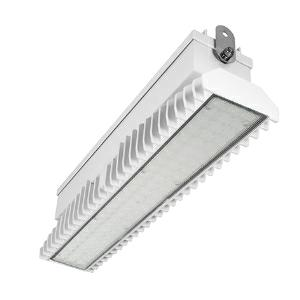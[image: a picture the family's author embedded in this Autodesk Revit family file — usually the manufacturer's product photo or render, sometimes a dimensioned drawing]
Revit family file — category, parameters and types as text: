
# Revit family: 3f_filippi_-_3f_lem_concentrato_3f_filippi_-_58887_a0812_-_3f_lem_1_led_50_cr_conc___vs_6c7b
name_source: partatom
category: Lighting Fixtures
units: mm (PartAtom-declared; Revit-internal decimal feet)

## family parameters
Cut with Voids When Loaded = No
Host = Face
Light Source = No
Part Type = Normal
Room Calculation Point = No
Round Connector Dimension = Use Diameter
Shared = No

## types (1)
- 3F Filippi - 3F LEM Concentrato (1 x LED, 6607 lm, 56 W, 4000 K)
    Apparent Load = 56 VA
    Approval mark = CE
    CIE Flux Codes = 78 93 98 100 100
    Color Rendering = 80
    Color Temperature = 4000 K
    Control Gear = Electronic ballast
    Default Elevation = 1800 mm
    Description = Industrial luminaire with high light output and high luminous efficiency designed with the most innovative technologies for environments with temperature up to 55°C.

ILLUMINOTECHNICAL
Luminous efficiency 100% (DLOR 98%, ULOR 2%).
Initial luminous flux of the luminaire 6607 lm.
Direct symmetric narrow distribution: the illuminated area has a elliptical shape.
Installation Interdistance Transv.D = 0.60 x hu - Long.D = 0.91 x hu.
Tabular UGR (CIE 117 - 4H-8H; S=0.25H; 70/50/20): RUG 23.3 - 24.5.
Beam angle: 38° - 61°.
Luminous efficacy 118 lm/W.
Lifetime (L93/B10): 30000 h. (tq+25°C)
Lifetime (L90/B10): 50000 h. (tq+25°C)
Lifetime (L85/B10): 80000 h. (tq+25°C)
Lifetime (L80/B10): 100000 h. (tq+25°C)
Lifetime (L85/B10): 50000 h. (tq+55°C)
Sudden decreased luminous flux after 50000 hours: 0% (C0).
Photobiological safety in compliance with IEC/TR 62778: RG0 risk exempt, (IEC 62471).
In compliance with IEC/EN 62722-2-1 - IEC/EN 62717 standards.

SOURCE
Mid-Power linear LED module 50W/840.
Energy efficiency class (UE 2019/2020 - UE 2019/2015): C.
CIE 13.3 Colour rendering index: CRI >80 (R9 <50%).
IES TM-30 Fidelity Index: Rf = 84 Rg = 95.
CCT nominal colour temperature 4000 K.
Colour initial tolerance (MacAdam): SDCM 3.

MECHANICAL
Passive modular heatsinks in die-casted aluminium, painted in white colour.
To optimize the thermal management of the LED module, the heatsinks are oversized and provided with self-cleaning of cooling fins.
Wiring body in aluminium and galvanised steel anchored solidly to the sinks and thermally separated.
3F Lens lenses with high luminous efficiency, transparent methacrylate (PMMA), fixed to the LED modules.
Fixing brackets in stainless steel.
Luminaire with limited surface temperature. - D - (EN 60598-2-24)
Dimensions: 542x115 mm, height 154 mm. Weight 6.385 kg.
IP65 protection degree.
Mechanical strength to impacts IK06 (1 joule).
Glow-wire test resistance 650°C.

ELECTRICAL
Halogen Free electronic wiring 230V-50/60Hz, power factor 0.95, THD <25%, constant output current, class I, 1 driver.
Power of the luminaire 56 W.
ENEC - CE.
SAFE FLICKER: PstLM=<1 and SVM=<0.4 (IEC TR 61547-1 and IEC TR 63158), to ensure a more comfortable and safe light.
Luminaire compliant with EN 60598-2-22 for power supply from a centralised emergency system CPSS (Central Power Supply System), not incorporated in the luminaire - high risk areas excluded. The default power and flux are 100% in AC and 100% in DC.
Ambient temperature from -30°C to +55°C.
Temperature class T6 max 85°C.
Quick connection via M20 3P connector with 9-13 mm tightening range.
Power unit positioned on a separate compartment by the LED module to ensure optimum temperatures of cabling components, to be inspectable and maintainable.
Relative humidity UR: <85%.

INSTALLATION
Ceiling / Suspended / Wall.
All accessories dedicated to this product are available on the Catalog and on our website www.3F-Filippi.com.

ACCESSORIES
A0812 - Anti-glare microprismatic VS moulded glass, tempered, not flammable, with sealing gasket.
One required for each light module. The pack contains 10 pieces.

APPLICATIONS
In commercial environments, exhibition and industrial areas, stores, open areas.
Applications with high ambient temperature up to 55°C.
Environments in which it is necessary a total protection against falling fragments (eg environments with foodstuffs or machines with moving parts or with extreme temperature changes), use luminaires with polycarbonate lenses.

WARNING
Fixture not suitable for cold stores with an ambient temperature <0°C and/or relative humidity >85%.
Luminaire designed for disposal/recycling at end-of-life.
Replaceable (LED only) light source by a professional. Replaceable control gear by a professional.
    Height = 154 mm
    Lamp = 1 x LED
    Lamp Light Flux = 6607 lm
    Lamp Power = 56 W
    Lamp count = 1
    Length = 542 mm
    Lifetime = 50000 h
    Luminous efficacy = 118 lm/W
    Manufacturer = 3F Filippi
    ModVariant = No
    Model = 3F Filippi - 58887+A0812 - 3F LEM 1 LED 50 CR CONC + VS
    Mounting Place = Ceiling
    Mounting Type = Pendant
    Number of Poles = 1
    OnlyDefault = Yes
    Power Factor = 1
    Product Name = 3F Filippi - 3F LEM Concentrato
    Product group = pendant luminaire
    ProductGroupID = 9
    Protection Class = Protection class I
    Protection Degree = IP 65
    RLX_Detail_Level = 1
    RLX_Emergency_Light_Flux = 0 lm
    RLX_Emergency_Type = 0
    RLX_Emergency_Type_DB = No
    RlxData = <blob elided: 90453 chars, md5=8e3efffb>
    Socket = socket
    Standby Power = 0 W
    System Light Flux = 6607 lm
    System Power = 56 W
    Type Comments = Product without accessories
    Type Image = 3f_filippi_-_lem_1__a0812.jpg
    URL = http://relux.com
    VarID = ---
    Voltage = 0 V
    Weight = 0.00 kg
    Width = 115 mm

## geometry (parser evidence)
native form markers: Blend x4, Sweep x14
no freeform markers — native parametric forms only
